# Revit family: QF_MOFFAT WALDORF_GPL8600E-CB
name_source: partatom
category: Specialty Equipment
revit_build: Autodesk Revit Architecture 2012 (Build: 20110916_2132(x64)
units: mm (PartAtom-declared; Revit-internal decimal feet)

## types (1)
- QF_MOFFAT WALDORF_GPL8600E-CB
    Apparent Power = 7200 VA
    Conn Conduit = Yes
    Cycle = 50 Hz
    Description = GRIDDLE PLATE LOW SPLASHBACK ELECTRIC ON CABINET BASE
    Elec Conn Connection Height = 0 mm  [stored 0 ft]
    Elec Conn RI Height = 0 mm  [stored 0 ft]
    FL Amps = 30 A
    Height = 970 mm  [stored 3.18241 ft]
    Manufacturer = MOFFAT WALDORF
    Max Overcurrent Protection = 0 A
    Min Ckt Ampacity = 0 A
    Model = GPL8600E-CB
    Number of Poles = 1
    Phase = 1
    URL = www.moffat.com
    URL Cutsheet = www.moffat.com
    Volts = 240 V
    Watts = 7200 W
    Weight in Pounds = 264.5544

note: [stored X ft] marks values corroborated as IEEE doubles in the binary element streams (Revit-internal decimal feet)

## geometry (parser evidence)
native form markers: Blend x10, Sweep x7
no freeform markers — native parametric forms only
